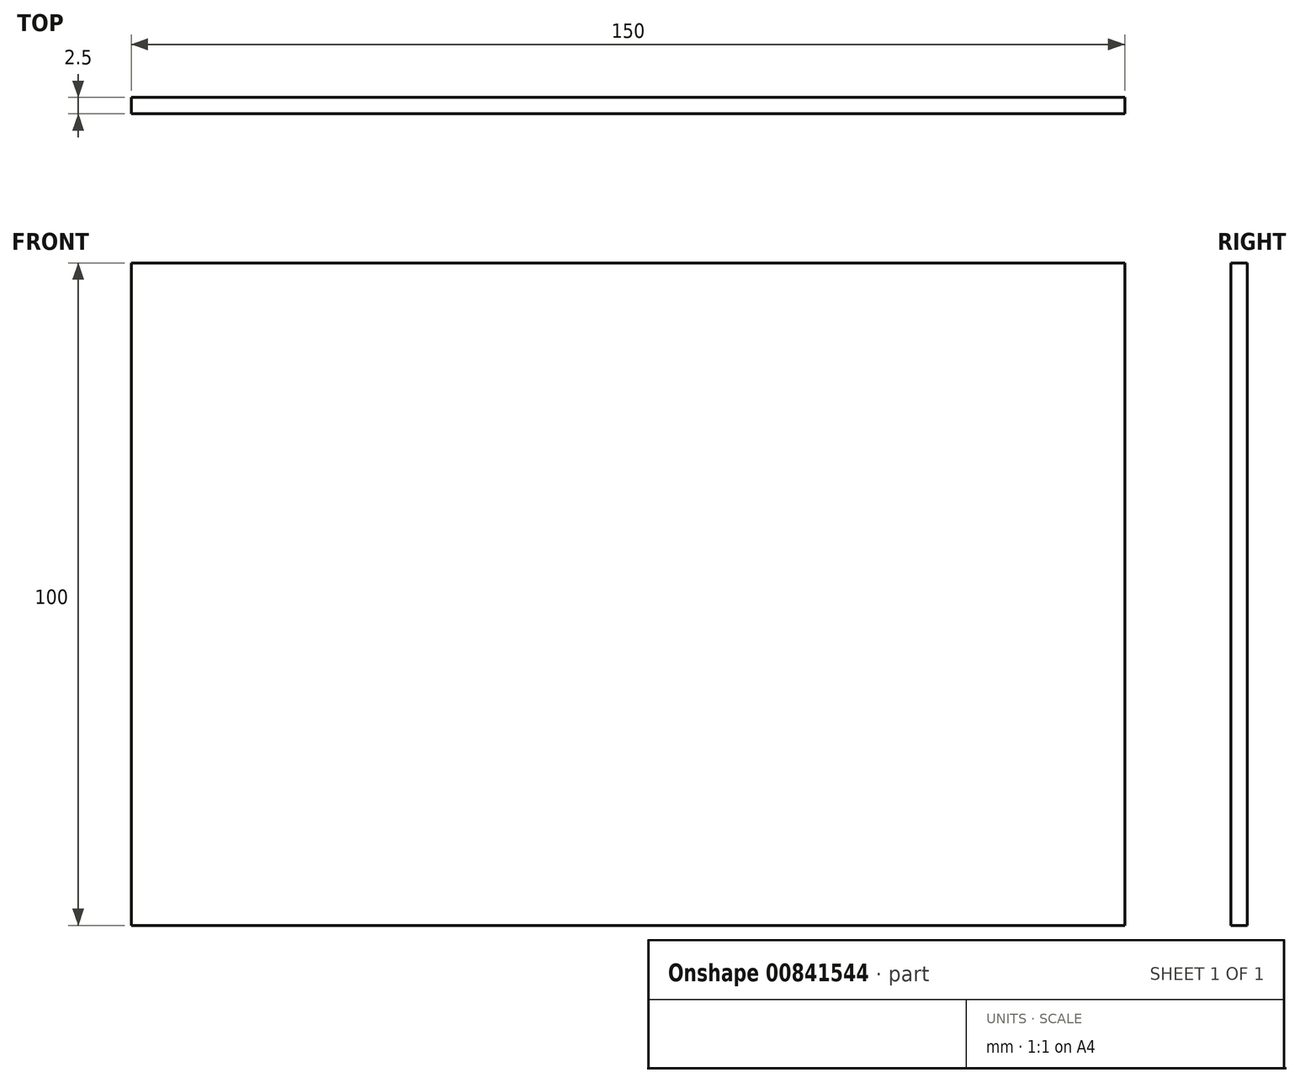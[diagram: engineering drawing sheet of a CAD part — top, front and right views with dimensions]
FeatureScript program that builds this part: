
annotation { "Feature Type Name" : "Feature", "Feature Type Description" : "" }
export const myFeature = defineFeature(function(context is Context, id is Id, definition is map)
    precondition{}
    {
        {
            var Q0;
            Q0=qCreatedBy(makeId("Front.planeOp"),FACE);
            var sketch = newSketch(context, id + "F0", { "sketchPlane" : qUnion([Q0])});
            skLineSegment(sketch, "E0.bottom", {"start": v(0, 0) * mm, "end": v(150, 0) * mm});
            skLineSegment(sketch, "E0.top", {"start": v(0, 100) * mm, "end": v(150, 100) * mm});
            skLineSegment(sketch, "E0.left", {"start": v(0, 0) * mm, "end": v(0, 100) * mm});
            skLineSegment(sketch, "E0.right", {"start": v(150, 0) * mm, "end": v(150, 100) * mm});
            skSolve(sketch);
        }
        {
            var Q0;
            Q0 = qSketchRegion(id + "F0", true);
            extrude(context, id + "F1", {"entities" : qUnion([Q0]), "depth" : 2.5 * mm, "offsetDistance" : 25 * mm});
        }
    });
